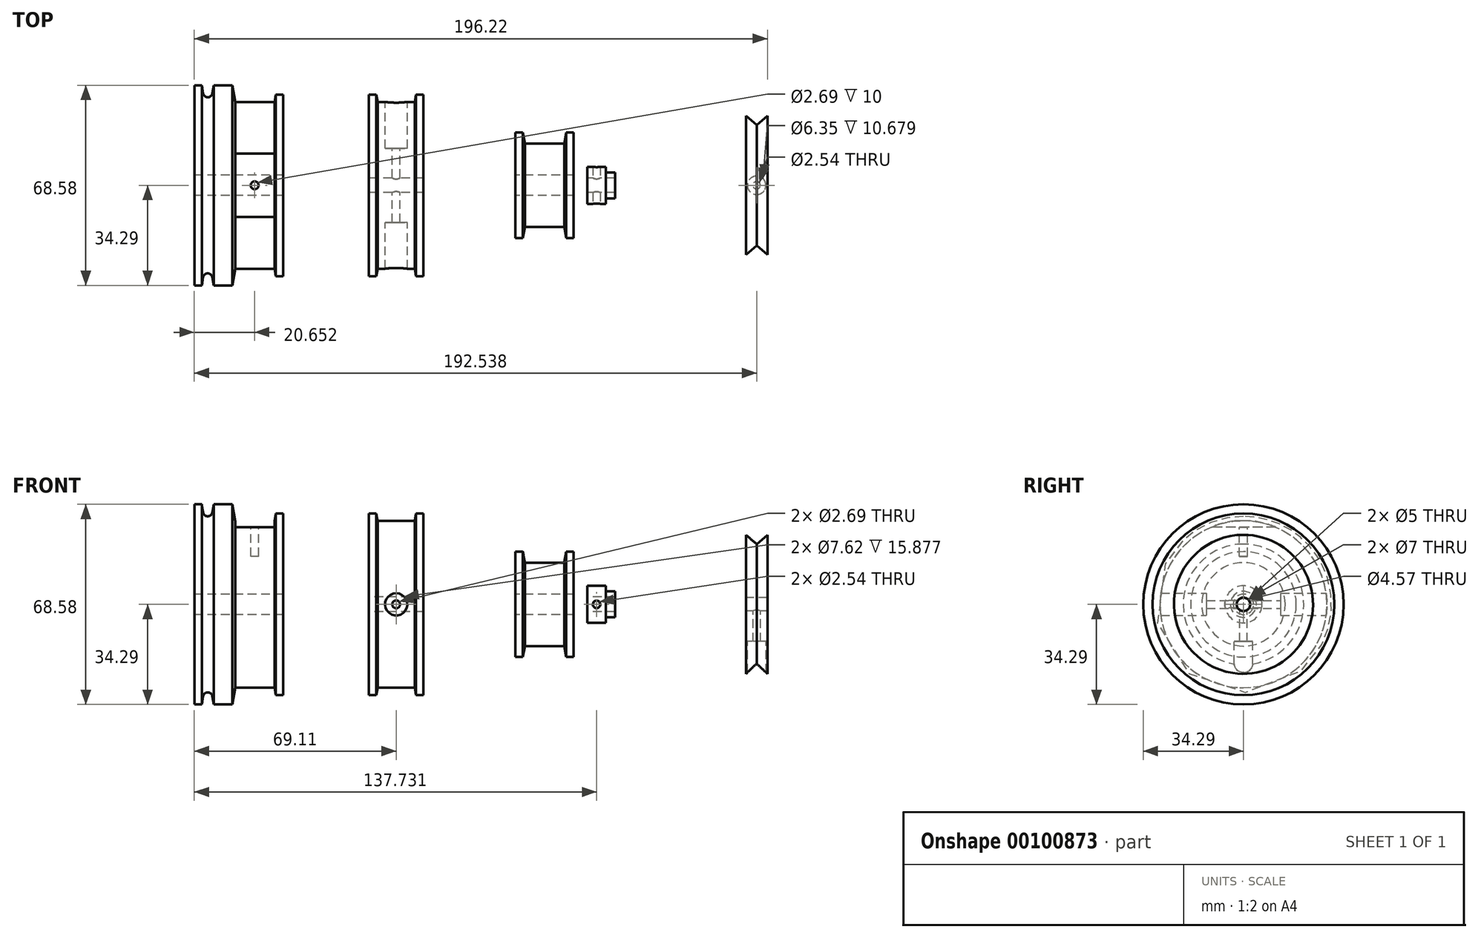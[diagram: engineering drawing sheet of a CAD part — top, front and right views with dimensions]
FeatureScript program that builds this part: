
annotation { "Feature Type Name" : "Feature", "Feature Type Description" : "" }
export const myFeature = defineFeature(function(context is Context, id is Id, definition is map)
    precondition{}
    {
        {
            var Q0;
            Q0=qCreatedBy(makeId("Front.planeOp"),FACE);
            var sketch = newSketch(context, id + "F0", { "sketchPlane" : qUnion([Q0])});
            skLineSegment(sketch, "E0", {"start": v(40.86, 3.5) * mm, "end": v(40.86, 18.06) * mm});
            skLineSegment(sketch, "E1", {"start": v(40.86, 18.06) * mm, "end": v(43.4, 18.06) * mm});
            skLineSegment(sketch, "E2", {"start": v(43.4, 18.06) * mm, "end": v(44.07, 14.29) * mm});
            skLineSegment(sketch, "E3", {"start": v(44.07, 14.29) * mm, "end": v(57.53, 14.29) * mm});
            skLineSegment(sketch, "E4", {"start": v(57.53, 14.29) * mm, "end": v(58.2, 18.06) * mm});
            skLineSegment(sketch, "E5", {"start": v(58.2, 18.06) * mm, "end": v(60.74, 18.06) * mm});
            skLineSegment(sketch, "E6", {"start": v(60.74, 18.06) * mm, "end": v(60.74, 3.5) * mm});
            skLineSegment(sketch, "E7", {"start": v(60.74, 3.5) * mm, "end": v(50.8, 3.5) * mm});
            skLineSegment(sketch, "E8", {"start": v(50.8, 3.5) * mm, "end": v(40.86, 3.5) * mm});
            skLineSegment(sketch, "E9", {"start": v(-8.38, 0) * mm, "end": v(9.48, 0) * mm, "construction": true});
            skSolve(sketch);
        }
        {
            var Q0;
            Q0 = qSketchRegion(id + "F0", true);
            var Q1;
            Q1=sQuery(id+"F0.wireOp",EDGE,"E9");
            revolve(context, id + "F1", {"entities" : qUnion([Q0]), "axis" : qUnion([Q1]), "revolveType" : RevolveType.FULL});
        }
        {
            var Q0;
            Q0=qCreatedBy(makeId("Front.planeOp"),FACE);
            var sketch = newSketch(context, id + "F2", { "sketchPlane" : qUnion([Q0])});
            skLineSegment(sketch, "E10", {"start": v(-69.1, -3.5) * mm, "end": v(-69.1, -34.29) * mm});
            skLineSegment(sketch, "E11", {"start": v(-55.1, -28.57) * mm, "end": v(-41.63, -28.57) * mm});
            skLineSegment(sketch, "E12", {"start": v(-38.64, -31.12) * mm, "end": v(-38.64, -3.5) * mm});
            skLineSegment(sketch, "E13", {"start": v(-38.64, -3.5) * mm, "end": v(-69.1, -3.5) * mm});
            skLineSegment(sketch, "E14", {"start": v(-41.63, -28.58) * mm, "end": v(-41.18, -31.12) * mm});
            skLineSegment(sketch, "E15", {"start": v(-41.18, -31.11) * mm, "end": v(-38.64, -31.11) * mm});
            skLineSegment(sketch, "E16", {"start": v(-53.67, 0) * mm, "end": v(-30.36, 0) * mm, "construction": true});
            skLineSegment(sketch, "E17", {"start": v(-55.1, -28.58) * mm, "end": v(-56.1, -34.29) * mm});
            skArc(sketch, "E18", {"start": v(-62.95, -31.47) * mm, "mid": v(-64.5, -30.16) * mm, "end": v(-66.07, -31.47) * mm});
            skLineSegment(sketch, "E19", {"start": v(-62.95, -31.47) * mm, "end": v(-62.45, -34.29) * mm});
            skLineSegment(sketch, "E20", {"start": v(-62.45, -34.3) * mm, "end": v(-56.1, -34.3) * mm});
            skLineSegment(sketch, "E21", {"start": v(-66.07, -31.47) * mm, "end": v(-66.57, -34.29) * mm});
            skLineSegment(sketch, "E22", {"start": v(-66.57, -34.29) * mm, "end": v(-69.1, -34.29) * mm});
            skSolve(sketch);
        }
        {
            var Q0;
            Q0 = qSketchRegion(id + "F2", true);
            var Q1;
            Q1=sQuery(id+"F2.wireOp",EDGE,"E16");
            revolve(context, id + "F3", {"entities" : qUnion([Q0]), "axis" : qUnion([Q1]), "revolveType" : RevolveType.FULL});
        }
        {
            var Q0;
            Q0=qCreatedBy(makeId("Front.planeOp"),FACE);
            var sketch = newSketch(context, id + "F4", { "sketchPlane" : qUnion([Q0])});
            skLineSegment(sketch, "E23", {"start": v(-41.65, 28.6) * mm, "end": v(-41.65, 26.45) * mm});
            skLineSegment(sketch, "E24", {"start": v(-41.65, 26.45) * mm, "end": v(-55.11, 26.45) * mm});
            skLineSegment(sketch, "E25", {"start": v(-55.11, 26.45) * mm, "end": v(-55.11, 28.6) * mm});
            skLineSegment(sketch, "E26", {"start": v(-55.11, 28.6) * mm, "end": v(-41.65, 28.6) * mm});
            skSolve(sketch);
        }
        {
            var Q0;
            Q0 = qSketchRegion(id + "F4", true);
            extrude(context, id + "F5", {"entities" : qUnion([Q0]), "operationType" : NewBodyOperationType.REMOVE, "endBound" : BoundingType.THROUGH_ALL, "oppositeDirection" : true, "depth" : 25.4 * mm, "hasSecondDirection" : true, "secondDirectionBound" : BoundingType.THROUGH_ALL, "secondDirectionOppositeDirection" : false, "secondDirectionDepth" : 25.4 * mm});
        }
        {
            var Q0;
            Q0=makeQuery(id+"F5.boolean.opBoolean","COPY",FACE,{"derivedFrom":makeQuery(id+"F5.opExtrude","SWEPT_FACE",FACE,{"disambiguationData":[OSD([sQuery(id+"F4.wireOp",EDGE,"E24")])]})});
            var sketch = newSketch(context, id + "F6", { "sketchPlane" : qUnion([Q0])});
            skCircle(sketch, "E27", {"center": v(-48.46, 0) * mm, "radius": 1.35 * mm});
            skSolve(sketch);
        }
        {
            var Q0;
            Q0=makeQuery(id+"F6.imprint","IMPRINT",FACE,{"disambiguationData":[TD([[makeQuery(id+"F6.imprint","IMPRINT",EDGE,{"derivedFrom":sQuery(id+"F6.wireOp",EDGE,"E27")}),1.0]])]});
            var Q1;
            Q1=sQuery(id+"FHP6A9VVXkGREsq_3.wireOp",EDGE,"nQaEFDUX-vHLL-KtvO-qypO-dfcL38EV3Zfl");
            extrude(context, id + "F7", {"entities" : qUnion([Q0]), "operationType" : NewBodyOperationType.REMOVE, "surfaceEntities" : qUnion([Q1]), "oppositeDirection" : true, "depth" : 10 * mm});
        }
        {
            var Q0;
            Q0=qCreatedBy(makeId("Front.planeOp"),FACE);
            var sketch = newSketch(context, id + "F8", { "sketchPlane" : qUnion([Q0])});
            skLineSegment(sketch, "E28", {"start": v(9.34, 2.5) * mm, "end": v(-9.34, 2.5) * mm});
            skLineSegment(sketch, "E29", {"start": v(-9.34, 2.5) * mm, "end": v(-9.34, 31.12) * mm});
            skLineSegment(sketch, "E30", {"start": v(-9.34, 31.12) * mm, "end": v(-6.8, 31.12) * mm});
            skLineSegment(sketch, "E31", {"start": v(-6.8, 31.12) * mm, "end": v(-6.35, 28.58) * mm});
            skLineSegment(sketch, "E32", {"start": v(-6.35, 28.58) * mm, "end": v(6.35, 28.58) * mm});
            skLineSegment(sketch, "E33", {"start": v(6.35, 28.58) * mm, "end": v(6.8, 31.12) * mm});
            skLineSegment(sketch, "E34", {"start": v(6.8, 31.12) * mm, "end": v(9.34, 31.12) * mm});
            skLineSegment(sketch, "E35", {"start": v(0, 0) * mm, "end": v(0, 28.58) * mm, "construction": true});
            skLineSegment(sketch, "E36", {"start": v(0, 0) * mm, "end": v(10.46, 0) * mm, "construction": true});
            skLineSegment(sketch, "E37", {"start": v(9.34, 2.5) * mm, "end": v(9.34, 31.12) * mm});
            skSolve(sketch);
        }
        {
            var Q0;
            Q0=makeQuery(id+"F8.imprint","IMPRINT",FACE,{"disambiguationData":[TD([[makeQuery(id+"F8.imprint","IMPRINT",EDGE,{"derivedFrom":sQuery(id+"F8.wireOp",EDGE,"E28")}),-1.0]])]});
            var Q1;
            Q1=sQuery(id+"F8.wireOp",EDGE,"E36");
            revolve(context, id + "F9", {"entities" : qUnion([Q0]), "axis" : qUnion([Q1]), "revolveType" : RevolveType.FULL});
        }
        {
            var Q0;
            Q0=qCreatedBy(makeId("Right.planeOp"),FACE);
            var sketch = newSketch(context, id + "F10", { "sketchPlane" : qUnion([Q0])});
            skLineSegment(sketch, "E38", {"start": v(-34.81, 0) * mm, "end": v(39.5, 0) * mm, "construction": true});
            skLineSegment(sketch, "E39", {"start": v(0, 0) * mm, "end": v(38.1, 0) * mm});
            skLineSegment(sketch, "E40", {"start": v(38.1, 0) * mm, "end": v(38.1, 3.81) * mm});
            skLineSegment(sketch, "E41", {"start": v(38.1, 3.81) * mm, "end": v(12.7, 3.81) * mm});
            skLineSegment(sketch, "E42", {"start": v(12.7, 3.81) * mm, "end": v(12.7, 1.35) * mm});
            skLineSegment(sketch, "E43", {"start": v(12.7, 1.35) * mm, "end": v(-12.7, 1.35) * mm});
            skLineSegment(sketch, "E44", {"start": v(-12.7, 1.35) * mm, "end": v(-12.7, 3.8) * mm});
            skLineSegment(sketch, "E45", {"start": v(-12.7, 3.8) * mm, "end": v(-38.1, 3.8) * mm});
            skLineSegment(sketch, "E46", {"start": v(-38.1, 3.8) * mm, "end": v(-38.1, 0) * mm});
            skLineSegment(sketch, "E47", {"start": v(-38.1, 0) * mm, "end": v(0, 0) * mm});
            skLineSegment(sketch, "E48", {"start": v(0, 1.35) * mm, "end": v(0, 0) * mm, "construction": true});
            skSolve(sketch);
        }
        {
            var Q0;
            Q0 = qSketchRegion(id + "F10", true);
            var Q1;
            Q1=sQuery(id+"F10.wireOp",EDGE,"E38");
            revolve(context, id + "F11", {"operationType" : NewBodyOperationType.REMOVE, "entities" : qUnion([Q0]), "axis" : qUnion([Q1]), "revolveType" : RevolveType.FULL, "oppositeDirection" : true});
        }
        {
            var Q0;
            Q0=qCreatedBy(makeId("Front.planeOp"),FACE);
            var sketch = newSketch(context, id + "F12", { "sketchPlane" : qUnion([Q0])});
            skLineSegment(sketch, "E49", {"start": v(74.97, 2.5) * mm, "end": v(74.97, 4.45) * mm});
            skLineSegment(sketch, "E50", {"start": v(74.97, 4.45) * mm, "end": v(71.8, 4.45) * mm});
            skLineSegment(sketch, "E51", {"start": v(71.8, 4.44) * mm, "end": v(71.8, 6.35) * mm});
            skLineSegment(sketch, "E52", {"start": v(71.8, 6.35) * mm, "end": v(65.45, 6.35) * mm});
            skLineSegment(sketch, "E53", {"start": v(65.45, 6.35) * mm, "end": v(65.45, 2.5) * mm});
            skLineSegment(sketch, "E54", {"start": v(65.45, 2.5) * mm, "end": v(74.97, 2.5) * mm});
            skLineSegment(sketch, "E55", {"start": v(62.13, 0) * mm, "end": v(74.4, 0) * mm, "construction": true});
            skSolve(sketch);
        }
        {
            var Q0;
            Q0 = qSketchRegion(id + "F12", true);
            var Q1;
            Q1=sQuery(id+"F12.wireOp",EDGE,"E55");
            revolve(context, id + "F13", {"entities" : qUnion([Q0]), "axis" : qUnion([Q1]), "revolveType" : RevolveType.FULL});
        }
        {
            var Q0;
            Q0=qCreatedBy(makeId("Front.planeOp"),FACE);
            var sketch = newSketch(context, id + "F14", { "sketchPlane" : qUnion([Q0])});
            skCircle(sketch, "E56", {"center": v(68.62, 0) * mm, "radius": 1.27 * mm});
            skSolve(sketch);
        }
        {
            var Q0;
            Q0 = qSketchRegion(id + "F14", true);
            var Q1;
            Q1=sQuery(id+"F14.wireOp",EDGE,"E56");
            extrude(context, id + "F15", {"entities" : qUnion([Q0]), "operationType" : NewBodyOperationType.REMOVE, "surfaceEntities" : qUnion([Q1]), "endBound" : BoundingType.THROUGH_ALL, "oppositeDirection" : true, "depth" : 25.4 * mm, "hasSecondDirection" : true, "secondDirectionBound" : BoundingType.THROUGH_ALL, "secondDirectionOppositeDirection" : false, "secondDirectionDepth" : 25.4 * mm});
        }
        {
            var Q0;
            Q0=qCreatedBy(makeId("Front.planeOp"),FACE);
            var sketch = newSketch(context, id + "F16", { "sketchPlane" : qUnion([Q0])});
            skLineSegment(sketch, "E57", {"start": v(127.11, 23.81) * mm, "end": v(123.43, 20.64) * mm});
            skLineSegment(sketch, "E58", {"start": v(123.43, 20.64) * mm, "end": v(119.74, 23.81) * mm});
            skLineSegment(sketch, "E59", {"start": v(80.91, 0) * mm, "end": v(127.11, 0) * mm, "construction": true});
            skLineSegment(sketch, "E60", {"start": v(127.11, 23.81) * mm, "end": v(127.11, 2.29) * mm});
            skLineSegment(sketch, "E61", {"start": v(127.11, 2.29) * mm, "end": v(119.74, 2.29) * mm});
            skLineSegment(sketch, "E62", {"start": v(119.74, 2.29) * mm, "end": v(119.74, 23.81) * mm});
            skSolve(sketch);
        }
        {
            var Q0;
            Q0 = qSketchRegion(id + "F16", true);
            var Q1;
            Q1=sQuery(id+"F16.wireOp",EDGE,"E59");
            revolve(context, id + "F17", {"entities" : qUnion([Q0]), "axis" : qUnion([Q1]), "revolveType" : RevolveType.FULL});
        }
        {
            var Q0;
            Q0=makeQuery(id+"F17.opRevolve","SWEPT_FACE",FACE,{"disambiguationData":[OSD([sQuery(id+"F16.wireOp",EDGE,"E60")])]});
            var Q1;
            Q1=makeQuery(id+"F17.opRevolve","SWEPT_FACE",FACE,{"disambiguationData":[OSD([sQuery(id+"F16.wireOp",EDGE,"E62")])]});
            cPlane(context, id + "F18", {"entities" : qUnion([Q0, Q1]), "cplaneType" : CPlaneType.MID_PLANE, "offset" : 25.4 * mm, "width" : 152.4 * mm, "height" : 152.4 * mm});
        }
        {
            var Q0;
            Q0=qCreatedBy(id+"F18.planeOp",FACE);
            var sketch = newSketch(context, id + "F19", { "sketchPlane" : qUnion([Q0])});
            skLineSegment(sketch, "E63", {"start": v(1.27, 0) * mm, "end": v(1.27, -12.7) * mm});
            skLineSegment(sketch, "E64", {"start": v(1.27, -12.7) * mm, "end": v(3.18, -12.7) * mm});
            skLineSegment(sketch, "E65", {"start": v(3.18, -12.7) * mm, "end": v(3.18, -27.14) * mm});
            skLineSegment(sketch, "E66", {"start": v(3.18, -27.14) * mm, "end": v(0, -27.14) * mm});
            skLineSegment(sketch, "E67", {"start": v(0, -27.14) * mm, "end": v(0, 0) * mm});
            skLineSegment(sketch, "E68", {"start": v(0, 0) * mm, "end": v(1.27, 0) * mm});
            skLineSegment(sketch, "E69", {"start": v(0, 0) * mm, "end": v(0, 18.97) * mm, "construction": true});
            skSolve(sketch);
        }
        {
            var Q0;
            Q0=makeQuery(id+"F19.imprint","IMPRINT",FACE,{"disambiguationData":[TD([[makeQuery(id+"F19.imprint","IMPRINT",EDGE,{"derivedFrom":sQuery(id+"F19.wireOp",EDGE,"E63")}),-1.0]])]});
            var Q1;
            Q1=sQuery(id+"F19.wireOp",EDGE,"E69");
            var Q2;
            Q2=sQuery(id+"F19.wireOp",EDGE,"E69");
            revolve(context, id + "F20", {"operationType" : NewBodyOperationType.REMOVE, "entities" : qUnion([Q0]), "surfaceEntities" : qUnion([Q1]), "axis" : qUnion([Q2]), "revolveType" : RevolveType.FULL, "oppositeDirection" : true});
        }
    });
